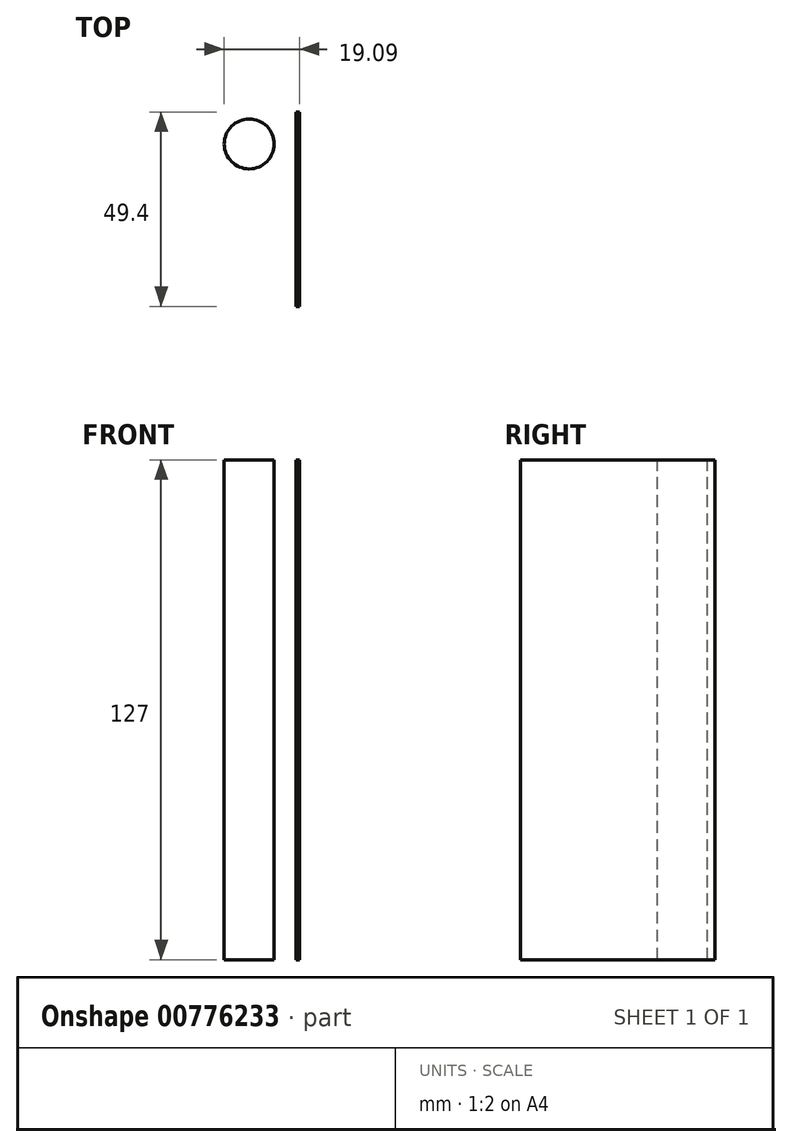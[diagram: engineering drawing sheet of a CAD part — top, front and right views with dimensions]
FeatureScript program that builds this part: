
annotation { "Feature Type Name" : "Feature", "Feature Type Description" : "" }
export const myFeature = defineFeature(function(context is Context, id is Id, definition is map)
    precondition{}
    {
        {
            var Q0;
            Q0=qCreatedBy(makeId("Top.planeOp"),FACE);
            var sketch = newSketch(context, id + "F0", { "sketchPlane" : qUnion([Q0])});
            skLineSegment(sketch, "E0", {"start": v(-46.57, 25.42) * mm, "end": v(-46.57, -23.98) * mm});
            skLineSegment(sketch, "E1", {"start": v(-46.57, -23.98) * mm, "end": v(47.5, -23.98) * mm});
            skLineSegment(sketch, "E2", {"start": v(47.5, -23.98) * mm, "end": v(47.5, 25.42) * mm});
            skLineSegment(sketch, "E3", {"start": v(47.5, 25.42) * mm, "end": v(-46.57, 25.42) * mm});
            skSolve(sketch);
        }
        {
            var Q0;
            Q0=makeQuery(id+"F0.imprint","IMPRINT",FACE,{"disambiguationData":[TD([[makeQuery(id+"F0.imprint","IMPRINT",EDGE,{"derivedFrom":sQuery(id+"F0.wireOp",EDGE,"E0")}),1.0]])]});
            extrude(context, id + "F1", {"entities" : qUnion([Q0]), "depth" : 127 * mm, "offsetDistance" : 25.4 * mm});
        }
        {
            var Q0;
            Q0=makeQuery(id+"F1.opExtrude","CAP_FACE",FACE,{"disambiguationData":[OSD([sQuery(id+"F0.wireOp",EDGE,"E0"),sQuery(id+"F0.wireOp",EDGE,"E1"),sQuery(id+"F0.wireOp",EDGE,"E2"),sQuery(id+"F0.wireOp",EDGE,"E3")])],"isStart":false});
            var sketch = newSketch(context, id + "F2", { "sketchPlane" : qUnion([Q0])});
            skLineSegment(sketch, "E4.bottom", {"start": v(-29.23, 13.34) * mm, "end": v(-40.27, 13.34) * mm});
            skLineSegment(sketch, "E4.top", {"start": v(-29.23, 21.22) * mm, "end": v(-40.27, 21.22) * mm});
            skLineSegment(sketch, "E4.left", {"start": v(-29.23, 13.34) * mm, "end": v(-29.23, 21.22) * mm});
            skLineSegment(sketch, "E4.right", {"start": v(-40.27, 13.34) * mm, "end": v(-40.27, 21.22) * mm});
            skPoint(sketch, "E4.middle", {"position": v(-34.75, 17.28) * mm});
            skSolve(sketch);
        }
        {
            var Q0;
            Q0=sQuery(id+"F2.wireOp",VERTEX,"E4.middle");
            var Q1;
            Q1=makeQuery(id+"F1.opExtrude","SWEPT_BODY",BODY,{"disambiguationData":[OSD([sQuery(id+"F0.wireOp",EDGE,"E0"),sQuery(id+"F0.wireOp",EDGE,"E1"),sQuery(id+"F0.wireOp",EDGE,"E2"),sQuery(id+"F0.wireOp",EDGE,"E3")])]});
            hole(context, id + "F3", {"style" : HoleStyle.SIMPLE, "endStyle" : HoleEndStyle.THROUGH, "holeDiameter" : 12.7 * mm, "majorDiameter" : 6.35 * mm, "isTappedThrough" : true, "tappedDepth" : 12.7 * mm, "tapClearance" : 3, "locations" : qUnion([Q0]), "scope" : qUnion([Q1])});
        }
        {
            var Q0;
            Q0=makeQuery(id+"F1.opExtrude","SWEPT_BODY",BODY,{"disambiguationData":[OSD([sQuery(id+"F0.wireOp",EDGE,"E0"),sQuery(id+"F0.wireOp",EDGE,"E1"),sQuery(id+"F0.wireOp",EDGE,"E2"),sQuery(id+"F0.wireOp",EDGE,"E3")])]});
            var Q1;
            Q1=qCreatedBy(makeId("Right.planeOp"),FACE);
            mirror(context, id + "F4", {"operationType" : NewBodyOperationType.REMOVE, "entities" : qUnion([Q0]), "mirrorPlane" : qUnion([Q1])});
        }
    });
